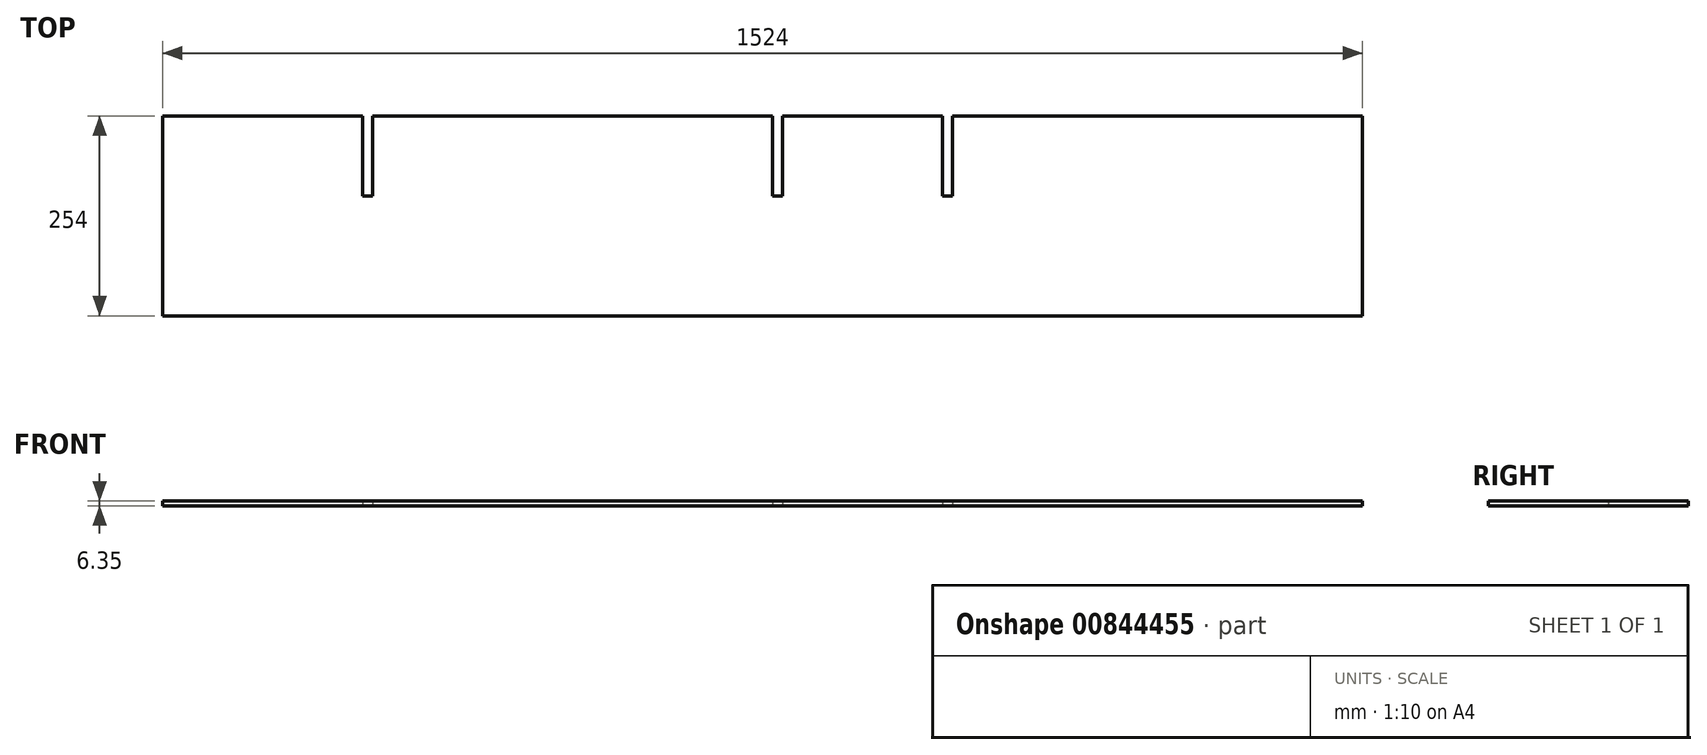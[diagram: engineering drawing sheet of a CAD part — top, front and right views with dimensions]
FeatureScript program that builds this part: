
annotation { "Feature Type Name" : "Feature", "Feature Type Description" : "" }
export const myFeature = defineFeature(function(context is Context, id is Id, definition is map)
    precondition{}
    {
        {
            var Q0;
            Q0=qCreatedBy(makeId("Top.planeOp"),FACE);
            var sketch = newSketch(context, id + "F0", { "sketchPlane" : qUnion([Q0])});
            skLineSegment(sketch, "E0.bottom", {"start": v(-762, 127) * mm, "end": v(762, 127) * mm});
            skLineSegment(sketch, "E0.top", {"start": v(-762, -127) * mm, "end": v(762, -127) * mm});
            skLineSegment(sketch, "E0.left", {"start": v(-762, 127) * mm, "end": v(-762, -127) * mm});
            skLineSegment(sketch, "E0.right", {"start": v(762, 127) * mm, "end": v(762, -127) * mm});
            skLineSegment(sketch, "E1", {"start": v(-508, 127) * mm, "end": v(-508, 25.4) * mm});
            skLineSegment(sketch, "E2", {"start": v(-508, 25.4) * mm, "end": v(-495.3, 25.4) * mm});
            skLineSegment(sketch, "E3", {"start": v(-495.3, 25.4) * mm, "end": v(-495.3, 127) * mm});
            skLineSegment(sketch, "E4", {"start": v(-495.3, 127) * mm, "end": v(-508, 127) * mm});
            skLineSegment(sketch, "E5", {"start": v(12.7, 127) * mm, "end": v(12.7, 25.4) * mm});
            skLineSegment(sketch, "E6", {"start": v(12.7, 25.4) * mm, "end": v(25.4, 25.4) * mm});
            skLineSegment(sketch, "E7", {"start": v(25.4, 25.4) * mm, "end": v(25.4, 127) * mm});
            skLineSegment(sketch, "E8", {"start": v(25.4, 127) * mm, "end": v(12.7, 127) * mm});
            skLineSegment(sketch, "E9", {"start": v(228.6, 127) * mm, "end": v(228.6, 25.4) * mm});
            skLineSegment(sketch, "E10", {"start": v(228.6, 25.4) * mm, "end": v(241.3, 25.4) * mm});
            skLineSegment(sketch, "E11", {"start": v(241.3, 25.4) * mm, "end": v(241.3, 127) * mm});
            skLineSegment(sketch, "E12", {"start": v(241.3, 127) * mm, "end": v(228.6, 127) * mm});
            skSolve(sketch);
        }
        {
            var Q0;
            Q0=makeQuery(id+"F0.imprint","IMPRINT",FACE,{"disambiguationData":[TD([[makeQuery(id+"F0.imprint","IMPRINT",EDGE,{"derivedFrom":sQuery(id+"F0.wireOp",EDGE,"E0.top")}),1.0]])]});
            extrude(context, id + "F1", {"entities" : qUnion([Q0]), "depth" : 6.35 * mm, "offsetDistance" : 25.4 * mm});
        }
    });
